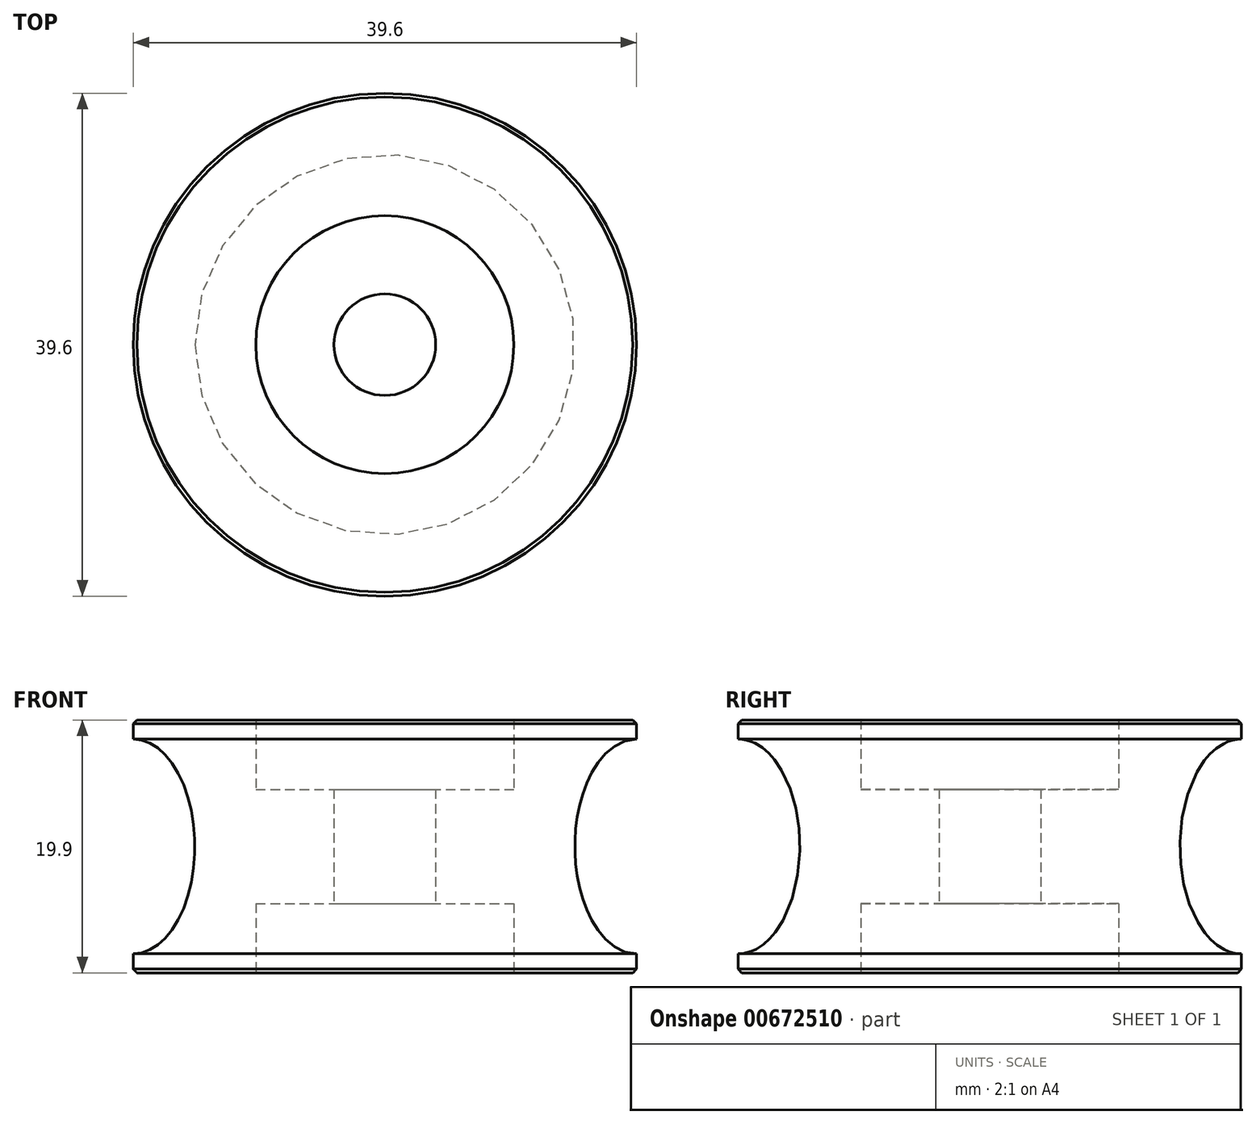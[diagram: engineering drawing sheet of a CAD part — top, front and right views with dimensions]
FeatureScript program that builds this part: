
annotation { "Feature Type Name" : "Feature", "Feature Type Description" : "" }
export const myFeature = defineFeature(function(context is Context, id is Id, definition is map)
    precondition{}
    {
        {
            var Q0;
            Q0=qCreatedBy(makeId("Front.planeOp"),FACE);
            var sketch = newSketch(context, id + "F0", { "sketchPlane" : qUnion([Q0])});
            skLineSegment(sketch, "E0", {"start": v(0, 0) * mm, "end": v(0, 4.5) * mm, "construction": true});
            skLineSegment(sketch, "E1", {"start": v(10.15, 9.95) * mm, "end": v(19.8, 9.95) * mm});
            skLineSegment(sketch, "E2", {"start": v(19.8, 9.95) * mm, "end": v(19.8, 8.45) * mm});
            skLineSegment(sketch, "E3", {"start": v(0, 4.5) * mm, "end": v(10.15, 4.5) * mm, "construction": true});
            skLineSegment(sketch, "E4", {"start": v(10.15, 4.5) * mm, "end": v(10.15, 9.95) * mm});
            skEllipticalArc(sketch, "E5", {});
            skPoint(sketch, "E6", {"position": v(14.95, 0) * mm});
            skLineSegment(sketch, "E7.MirrorCS", {"start": v(0, 0) * mm, "end": v(0, -4.5) * mm, "construction": true});
            skLineSegment(sketch, "E8.MirrorCS", {"start": v(0, -4.5) * mm, "end": v(10.15, -4.5) * mm, "construction": true});
            skLineSegment(sketch, "E9.MirrorCS", {"start": v(10.15, -4.5) * mm, "end": v(10.15, -9.95) * mm});
            skLineSegment(sketch, "E10.MirrorCS", {"start": v(10.15, -9.95) * mm, "end": v(19.8, -9.95) * mm});
            skLineSegment(sketch, "E11.MirrorCS", {"start": v(19.8, -9.95) * mm, "end": v(19.8, -8.45) * mm});
            skEllipticalArc(sketch, "E12.MirrorCS", {});
            skLineSegment(sketch, "E13", {"start": v(4, 4.5) * mm, "end": v(4, -4.5) * mm});
            skLineSegment(sketch, "E14", {"start": v(4, 4.5) * mm, "end": v(10.15, 4.5) * mm});
            skLineSegment(sketch, "E15", {"start": v(4, -4.5) * mm, "end": v(10.15, -4.5) * mm});
            const initialGuessF0  = {"E5": [0.0198, 0, 0, 1, 0.00845, 0.00485, 0, 1.5707963267948966], "E12.MirrorCS": [0.0198, 0, 0, -1, 0.00845, 0.00485, 4.71238898038469, 0]};
            skSetInitialGuess(sketch, initialGuessF0);
            skSolve(sketch);
        }
        {
            var Q0;
            Q0=makeQuery(id+"F0.imprint","IMPRINT",FACE,{"disambiguationData":[TD([[makeQuery(id+"F0.imprint","IMPRINT",EDGE,{"derivedFrom":sQuery(id+"F0.wireOp",EDGE,"E1")}),-1.0]])]});
            var Q1;
            Q1=sQuery(id+"F0.wireOp",EDGE,"E0");
            revolve(context, id + "F1", {"surfaceOperationType" : NewSurfaceOperationType.NEW, "entities" : qUnion([Q0]), "axis" : qUnion([Q1]), "revolveType" : RevolveType.FULL});
        }
        {
            var Q0;
            Q0=makeQuery(id+"F1.opRevolve","SWEPT_EDGE",EDGE,{"disambiguationData":[OSD([sQuery(id+"F0.wireOp",EDGE,"E1"),sQuery(id+"F0.wireOp",EDGE,"E2")])]});
            var Q1;
            Q1=makeQuery(id+"F1.opRevolve","SWEPT_EDGE",EDGE,{"disambiguationData":[OSD([sQuery(id+"F0.wireOp",EDGE,"E10.MirrorCS"),sQuery(id+"F0.wireOp",EDGE,"E11.MirrorCS")])]});
            chamfer(context, id + "F2", {"entities" : qUnion([Q0, Q1]), "width" : 0.3 * mm, "tangentPropagation" : true});
        }
    });
